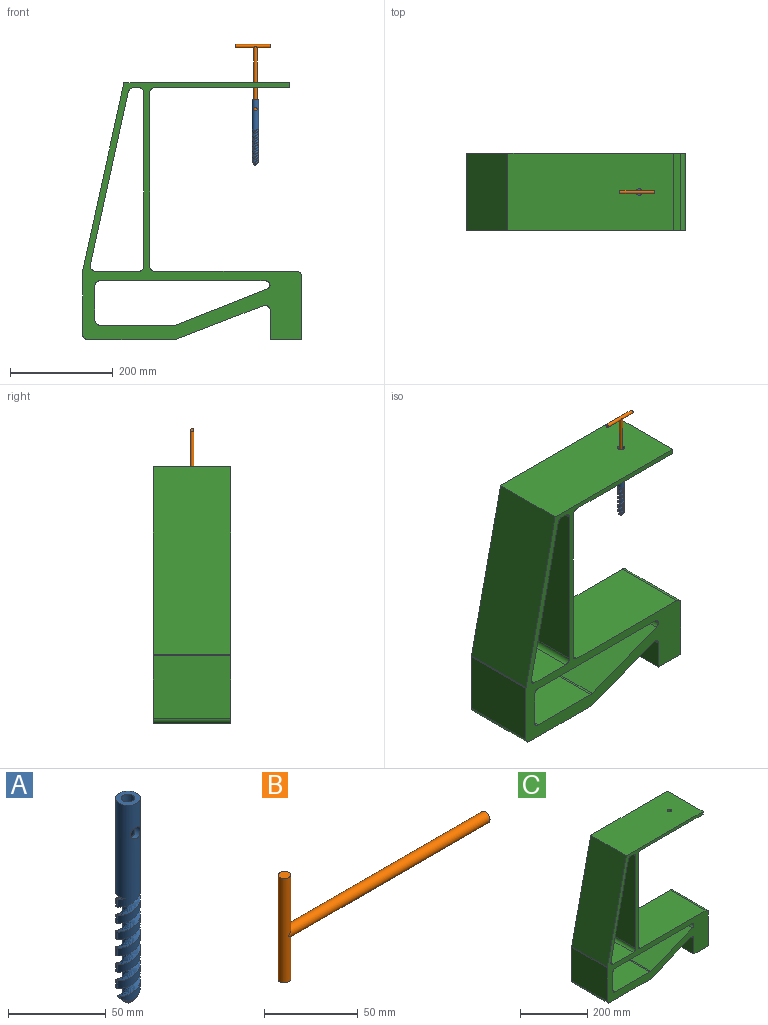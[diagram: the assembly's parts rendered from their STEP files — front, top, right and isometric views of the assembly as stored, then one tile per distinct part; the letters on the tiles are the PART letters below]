
ASSEMBLY  parts=3 mates=3
PART A: 20 faces, bbox 14.4x13.9x128.2 mm
  f0: cylinder r=6.35mm len=75.9mm, axis (0,0,-1), area 2435.3mm2, adj f1,f4,f7,f8,f9,f10,f11,f12
  f1: cylinder r=6.35mm len=25.1mm, axis (0,0,-1), area 190.6mm2, adj f0,f2,f10,f12
  f2: cylinder r=6.35mm len=25.1mm, axis (0,0,-1), area 190.6mm2, adj f1,f3,f10,f12
  f3: cylinder r=6.35mm len=12.52mm, axis (0,0,-1), area 72.9mm2, adj f2,f10,f12,f14
  f4: cylinder r=6.35mm len=25.1mm, axis (0,0,-1), area 190.6mm2, adj f0,f5,f9,f13
  f5: cylinder r=6.35mm len=25.1mm, axis (0,0,-1), area 190.6mm2, adj f4,f6,f9,f13
  f6: cylinder r=6.35mm len=20.32mm, axis (0,0,-1), area 168.1mm2, adj f5,f9,f13,f14
  f7: plane 12.7x12.7mm, normal (0,0,1), area 89.7mm2, adj f0,f15
  f8: plane 9.22x5.3mm, normal (0,0,-1), area 25mm2, adj f0,f9,f10
  f9: bspline ~69.09x13.32mm, area 588.3mm2, adj f0,f4,f5,f6,f8,f10,f14
  f10: bspline ~69.09x14.19mm, area 423.9mm2, adj f0,f1,f2,f3,f8,f9,f14
  f11: plane 9.22x5.3mm, normal (0,0,-1), area 25mm2, adj f0,f12,f13
  f12: bspline ~69.09x13.32mm, area 588.3mm2, adj f0,f1,f2,f3,f11,f13,f14
  f13: bspline ~69.09x14.19mm, area 423.9mm2, adj f0,f4,f5,f6,f11,f12,f14
  f14: cone r=6.35mm half-angle=45deg, axis (0,0,1), area 101.3mm2, adj f3,f6,f9,f10,f12,f13,f19
  f15: cylinder r=3.43mm len=17.43mm, axis (0,0,1), area 375.5mm2, adj f7,f16
  f16: cylinder r=3.56mm len=12.7mm, axis (0,-1,0), area 200.6mm2, adj f0,f15,f18
  f17: plane 6.86x6.86mm, normal (0,0,1), area 36.9mm2, adj f18
  f18: cylinder r=3.43mm len=36.85mm, axis (0,0,1), area 751.6mm2, adj f16,f17
  f19: cone r=0mm half-angle=50.9deg, axis (0,0,1), area 6.6mm2, adj f14
PART B: 7 faces, bbox 155.2x6.9x68.1 mm
  f0: plane 0.81x0.02mm, normal (-1,0,0), area 0mm2, adj f2,f5
  f1: plane 0.81x0.02mm, normal (-1,0,0), area 0mm2, adj f2,f5
  f2: cylinder r=3.43mm len=151.75mm, axis (-1,0,0), area 3224.9mm2, adj f0,f1,f3,f5
  f3: plane 6.86x6.86mm, normal (1,0,0), area 36.9mm2, adj f2
  f4: plane 6.81x6.81mm, normal (0,0,1), area 36.4mm2, adj f5
  f5: cylinder r=3.41mm len=68.08mm, axis (0,0,-1), area 1409.1mm2, adj f0,f1,f2,f4,f6
  f6: plane 6.81x6.81mm, normal (0,0,-1), area 36.4mm2, adj f5
PART C: 38 faces, bbox 425.7x150x500 mm
  f0: plane 336.97x150mm, normal (0.98,0,-0.21), area 51744.5mm2, adj f20,f21,f34,f37
  f1: plane 150x10.62mm, normal (0,0,-1), area 1593.4mm2, adj f20,f21,f34,f35
  f2: plane 336.97x150mm, normal (-1,0,0), area 50544.9mm2, adj f20,f21,f35,f36
  f3: plane 170.42x150mm, normal (0,0,-1), area 25563.5mm2, adj f4,f20,f21,f33
  f4: plane 170.96x150mm, normal (0.36,0,-0.93), area 27480.1mm2, adj f3,f20,f21,f28
  f5: plane 150x56.51mm, normal (-1,0,0), area 8476.9mm2, adj f6,f20,f21,f28
  f6: plane 150x60.69mm, normal (0,0,-1), area 9104mm2, adj f5,f7,f20,f21
  f7: plane 150x123.03mm, normal (1,0,0), area 18455.1mm2, adj f6,f20,f21,f29
  f8: plane 275.25x150mm, normal (0,0,1), area 41287mm2, adj f20,f21,f29,f30
  f9: plane 336.97x150mm, normal (1,0,0), area 50544.9mm2, adj f20,f21,f30,f31
  f10: plane 262.79x150mm, normal (0,0,-1), area 39281.3mm2, adj f11,f20,f21,f22,f31
  f11: plane 150x10mm, normal (1,0,0), area 1500mm2, adj f10,f12,f20,f21
  f12: plane 322.79x150mm, normal (0,0,1), area 48281.3mm2, adj f11,f13,f20,f21,f22
  f13: plane 365.91x150mm, normal (-0.98,0,0.21), area 56188.9mm2, adj f12,f20,f21,f32
  f14: plane 321.13x150mm, normal (0,0,-1), area 48168.9mm2, adj f20,f21,f24,f27
  f15: plane 176.45x150mm, normal (-0.37,0,0.93), area 28438.3mm2, adj f20,f21,f23,f25
  f16: plane 150x144.68mm, normal (0,0,1), area 21701.7mm2, adj f20,f21,f25,f26
  f17: plane 150x121.95mm, normal (-1,0,0), area 18292.6mm2, adj f20,f21,f32,f33
  f18: plane 150x66.54mm, normal (1,0,0), area 9980.7mm2, adj f20,f21,f26,f27
  f19: plane 150x84.47mm, normal (0,0,1), area 12670.7mm2, adj f20,f21,f36,f37
  f20: plane 500x425.67mm, normal (0,-1,0), area 39090.7mm2, adj f0,f1,f2,f3,f4,f5,f6,f7
  f21: plane 500x425.67mm, normal (0,1,0), area 39090.7mm2, adj f0,f1,f2,f3,f4,f5,f6,f7
  f22: cylinder r=6.6mm len=13.21mm, axis (0,0,1), area 415mm2, adj f10,f12
  f23: cylinder r=10mm len=150mm, axis (0,-1,0), area 1582.6mm2, adj f15,f20,f21,f24
  f24: cylinder r=10mm len=150mm, axis (0,-1,0), area 2144.3mm2, adj f14,f20,f21,f23
  f25: cylinder r=10mm len=150mm, axis (0,-1,0), area 561.8mm2, adj f15,f16,f20,f21
  f26: cylinder r=10mm len=150mm, axis (0,-1,0), area 2356.2mm2, adj f16,f18,f20,f21
  f27: cylinder r=10mm len=150mm, axis (0,-1,0), area 2356.2mm2, adj f14,f18,f20,f21
  f28: cylinder r=10mm len=150mm, axis (0,-1,0), area 2907.6mm2, adj f4,f5,f20,f21
  f29: cylinder r=10mm len=150mm, axis (0,1,0), area 2356.2mm2, adj f7,f8,f20,f21
  f30: cylinder r=10mm len=150mm, axis (0,-1,0), area 2356.2mm2, adj f8,f9,f20,f21
  f31: cylinder r=10mm len=150mm, axis (0,1,0), area 2356.2mm2, adj f9,f10,f20,f21
  f32: cylinder r=10mm len=150mm, axis (0,1,0), area 323.6mm2, adj f13,f17,f20,f21
  f33: cylinder r=10mm len=150mm, axis (0,1,0), area 2356.2mm2, adj f3,f17,f20,f21
  f34: cylinder r=10mm len=150mm, axis (0,-1,0), area 2032.6mm2, adj f0,f1,f20,f21
  f35: cylinder r=10mm len=150mm, axis (0,-1,0), area 2356.2mm2, adj f1,f2,f20,f21
  f36: cylinder r=10mm len=150mm, axis (0,-1,0), area 2356.2mm2, adj f2,f19,f20,f21
  f37: cylinder r=10mm len=150mm, axis (0,-1,0), area 2679.8mm2, adj f0,f19,f20,f21
PLACE A t=(188.69,-80.04,25.66)mm
PLACE B rot(axis=(0.71,0,-0.71),180deg) t=(218.74,-80.04,171.73)mm
PLACE C t=(8.65,-4.66,0.26)mm
MATE slider B.f2 <-> C.f22  axis (0,0,1) through (188.69,-80.04,180.84)mm
MATE revolute B.f2 <-> C.f22  axis (0,0,1) through (188.69,-80.04,180.84)mm
MATE slider A.f0 <-> C.f22  axis (0,0,-1) through (188.69,-80.04,152.66)mm
